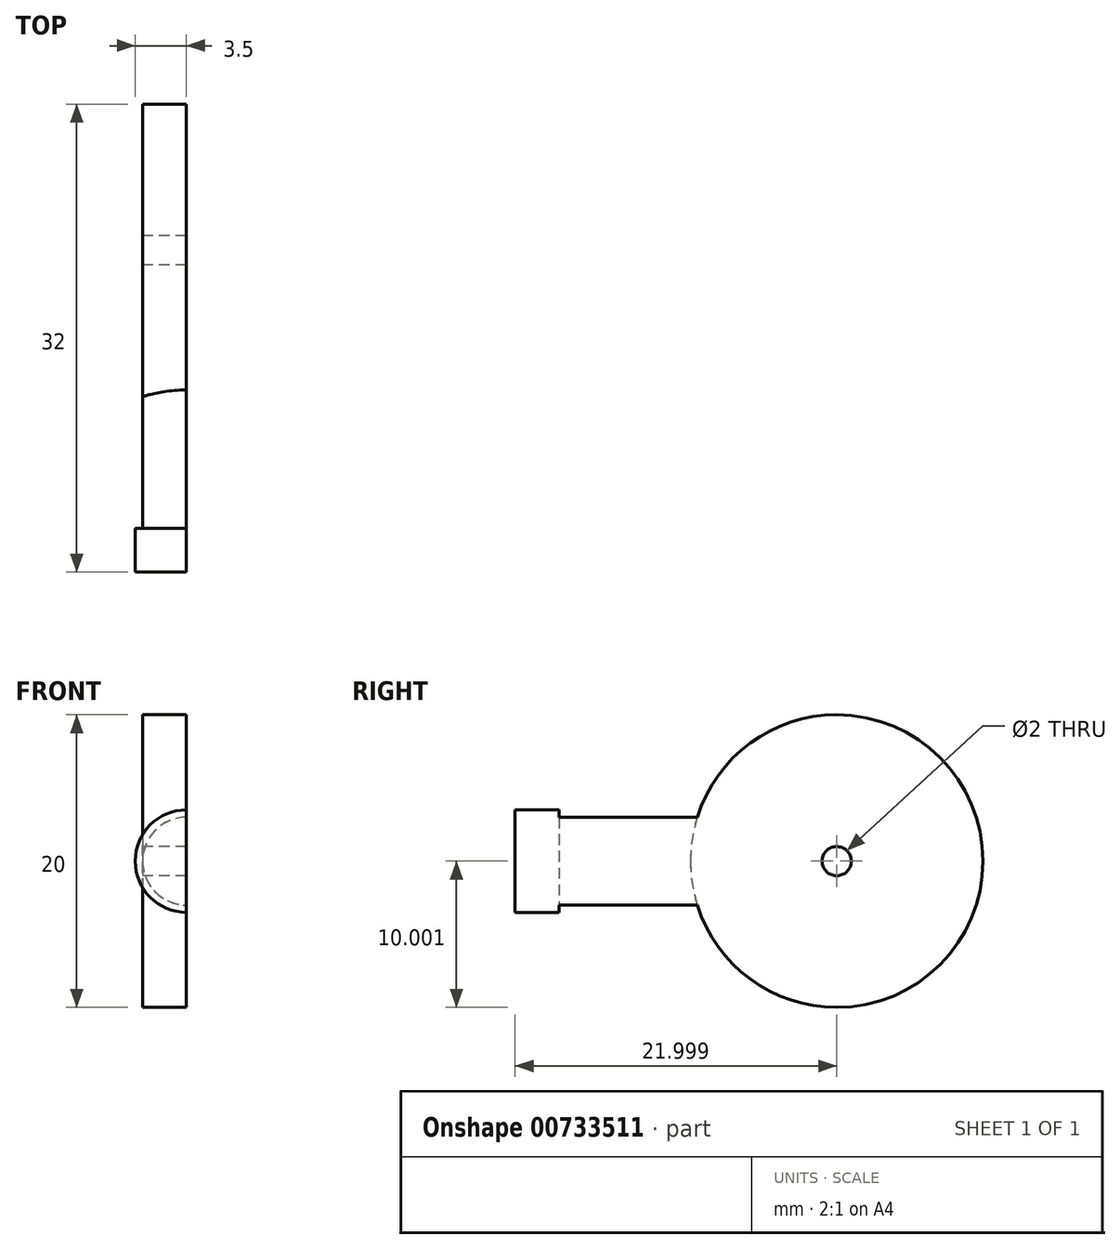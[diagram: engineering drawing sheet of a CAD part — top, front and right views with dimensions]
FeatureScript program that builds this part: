
annotation { "Feature Type Name" : "Feature", "Feature Type Description" : "" }
export const myFeature = defineFeature(function(context is Context, id is Id, definition is map)
    precondition{}
    {
        {
            var Q0;
            Q0=qCreatedBy(makeId("Right.planeOp"),FACE);
            var sketch = newSketch(context, id + "F0", { "sketchPlane" : qUnion([Q0])});
            skLineSegment(sketch, "E0.bottom", {"start": v(38.77, 35.28) * mm, "end": v(18.77, 35.28) * mm});
            skLineSegment(sketch, "E0.top", {"start": v(38.77, 15.28) * mm, "end": v(18.77, 15.28) * mm});
            skLineSegment(sketch, "E0.left", {"start": v(38.77, 35.28) * mm, "end": v(38.77, 15.28) * mm});
            skLineSegment(sketch, "E0.right", {"start": v(18.77, 35.28) * mm, "end": v(18.77, 15.28) * mm});
            skSolve(sketch);
        }
        {
            var Q0;
            Q0=makeQuery(id+"F0.imprint","IMPRINT",FACE,{"disambiguationData":[TD([[makeQuery(id+"F0.imprint","IMPRINT",EDGE,{"derivedFrom":sQuery(id+"F0.wireOp",EDGE,"E0.bottom")}),1.0]])]});
            extrude(context, id + "F1", {"entities" : qUnion([Q0]), "depth" : 3 * mm, "offsetDistance" : 25 * mm});
        }
        {
            var Q0;
            Q0=makeQuery(id+"F1.opExtrude","SWEPT_FACE",FACE,{"disambiguationData":[OSD([sQuery(id+"F0.wireOp",EDGE,"E0.right")])]});
            var sketch = newSketch(context, id + "F2", { "sketchPlane" : qUnion([Q0])});
            skCircle(sketch, "E1", {"center": v(3, 25.28) * mm, "radius": 3 * mm});
            skSolve(sketch);
        }
        {
            var Q0;
            {var subQ0=sQuery(id+"F2.wireOp",EDGE,"E1");var subQ1=sQuery(id+"F0.wireOp",EDGE,"E0.right");var subQ2=makeQuery(id+"F2.imprint","INTERSECT",VERTEX,{"derivedFrom":[makeQuery(id+"F1.opExtrude","CAP_EDGE",EDGE,{"disambiguationData":[OSD([subQ1])],"isStart":true}),subQ0]});Q0=makeQuery(id+"F2.imprint","IMPRINT",FACE,{"disambiguationData":[TD([[makeQuery(id+"F2.imprint","IMPRINT",EDGE,{"disambiguationData":[TD([[subQ2,1.0]])],"derivedFrom":subQ0}),1.0]])]});}
            extrude(context, id + "F3", {"entities" : qUnion([Q0]), "operationType" : NewBodyOperationType.ADD, "depth" : 9 * mm, "offsetDistance" : 25 * mm});
        }
        {
            var Q0;
            Q0=makeQuery(id+"F1.opExtrude","SWEPT_EDGE",EDGE,{"disambiguationData":[OSD([sQuery(id+"F0.wireOp",EDGE,"E0.bottom"),sQuery(id+"F0.wireOp",EDGE,"E0.left")])]});
            var Q1;
            Q1=makeQuery(id+"F1.opExtrude","SWEPT_EDGE",EDGE,{"disambiguationData":[OSD([sQuery(id+"F0.wireOp",EDGE,"E0.top"),sQuery(id+"F0.wireOp",EDGE,"E0.left")])]});
            fillet(context, id + "F4", {"entities" : qUnion([Q0, Q1]), "radius" : 10 * mm, "tangentPropagation" : true, "allowEdgeOverflow" : false});
        }
        {
            var Q0;
            Q0=makeQuery(id+"F1.opExtrude","SWEPT_EDGE",EDGE,{"disambiguationData":[OSD([sQuery(id+"F0.wireOp",EDGE,"E0.bottom"),sQuery(id+"F0.wireOp",EDGE,"E0.right")])]});
            var Q1;
            Q1=makeQuery(id+"F1.opExtrude","SWEPT_EDGE",EDGE,{"disambiguationData":[OSD([sQuery(id+"F0.wireOp",EDGE,"E0.top"),sQuery(id+"F0.wireOp",EDGE,"E0.right")])]});
            fillet(context, id + "F5", {"entities" : qUnion([Q0, Q1]), "radius" : 10 * mm, "tangentPropagation" : true, "allowEdgeOverflow" : false});
        }
        {
            var Q0;
            Q0=makeQuery(id+"F1.opExtrude","CAP_FACE",FACE,{"disambiguationData":[OSD([sQuery(id+"F0.wireOp",EDGE,"E0.bottom"),sQuery(id+"F0.wireOp",EDGE,"E0.top"),sQuery(id+"F0.wireOp",EDGE,"E0.left"),sQuery(id+"F0.wireOp",EDGE,"E0.right")])],"isStart":true});
            var sketch = newSketch(context, id + "F6", { "sketchPlane" : qUnion([Q0])});
            skCircle(sketch, "E2", {"center": v(-28.77, 25.28) * mm, "radius": 1 * mm});
            skSolve(sketch);
        }
        {
            var Q0;
            Q0=makeQuery(id+"F6.imprint","IMPRINT",FACE,{"disambiguationData":[TD([[makeQuery(id+"F6.imprint","IMPRINT",EDGE,{"derivedFrom":sQuery(id+"F6.wireOp",EDGE,"E2")}),1.0]])]});
            extrude(context, id + "F7", {"entities" : qUnion([Q0]), "operationType" : NewBodyOperationType.REMOVE, "oppositeDirection" : true, "depth" : 25 * mm, "offsetDistance" : 25 * mm});
        }
        {
            var Q0;
            Q0=makeQuery(id+"F3.opExtrude","CAP_FACE",FACE,{"disambiguationData":[OSD([sQuery(id+"F0.wireOp",EDGE,"E0.right"),sQuery(id+"F2.wireOp",EDGE,"E1")])],"isStart":false});
            var sketch = newSketch(context, id + "F8", { "sketchPlane" : qUnion([Q0])});
            skCircle(sketch, "E3", {"center": v(3, 25.28) * mm, "radius": 3.5 * mm});
            skLineSegment(sketch, "E4", {"start": v(3, 28.78) * mm, "end": v(3, 21.78) * mm});
            skSolve(sketch);
        }
        {
            var Q0;
            {var subQ4=makeQuery(id+"F3.opExtrude","CAP_EDGE",EDGE,{"disambiguationData":[OSD([sQuery(id+"F2.wireOp",EDGE,"E1")])],"isStart":false});Q0=makeQuery(id+"F8.imprint","IMPRINT",FACE,{"disambiguationData":[TD([[makeQuery(id+"F8.imprint","IMPRINT",EDGE,{"derivedFrom":subQ4}),-1.0]])]});}
            var Q1;
            {var subQ1=makeQuery(id+"F3.opExtrude","CAP_EDGE",EDGE,{"disambiguationData":[OSD([sQuery(id+"F2.wireOp",EDGE,"E1")])],"isStart":false});Q1=makeQuery(id+"F8.imprint","IMPRINT",FACE,{"disambiguationData":[TD([[makeQuery(id+"F8.imprint","IMPRINT",EDGE,{"derivedFrom":subQ1}),1.0]])]});}
            extrude(context, id + "F9", {"entities" : qUnion([Q0, Q1]), "operationType" : NewBodyOperationType.ADD, "depth" : 3 * mm, "offsetDistance" : 25 * mm});
        }
    });
